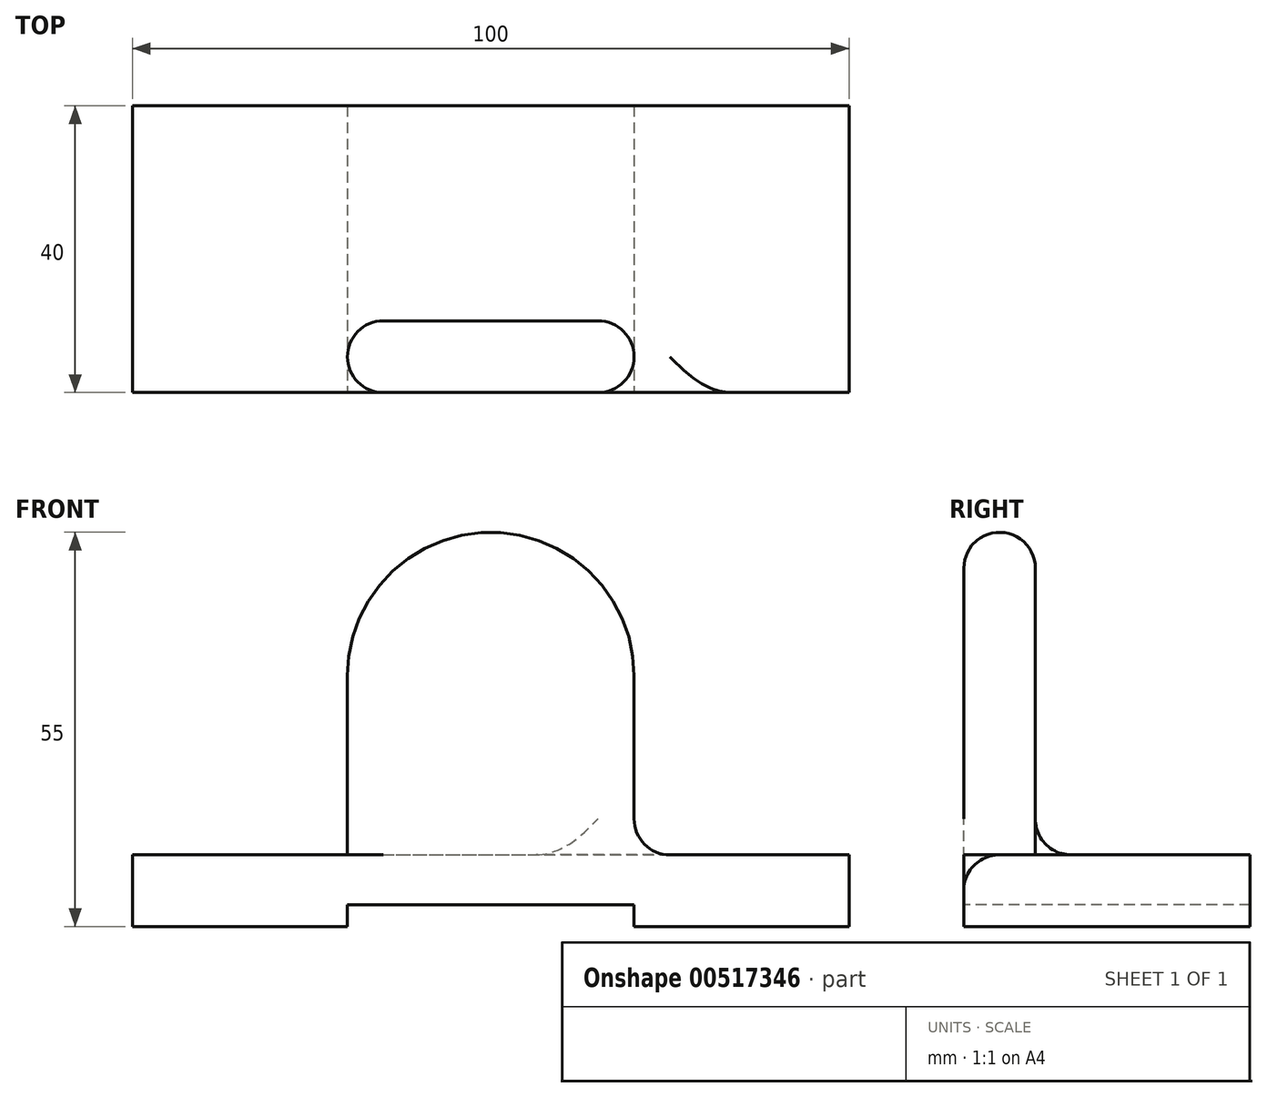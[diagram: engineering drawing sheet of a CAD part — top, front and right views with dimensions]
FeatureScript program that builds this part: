
annotation { "Feature Type Name" : "Feature", "Feature Type Description" : "" }
export const myFeature = defineFeature(function(context is Context, id is Id, definition is map)
    precondition{}
    {
        {
            var Q0;
            Q0=qCreatedBy(makeId("Top.planeOp"),FACE);
            var sketch = newSketch(context, id + "F0", { "sketchPlane" : qUnion([Q0])});
            skLineSegment(sketch, "E0.bottom", {"start": v(0, 0) * mm, "end": v(100, 0) * mm});
            skLineSegment(sketch, "E0.top", {"start": v(0, 40) * mm, "end": v(100, 40) * mm});
            skLineSegment(sketch, "E0.left", {"start": v(0, 0) * mm, "end": v(0, 40) * mm});
            skLineSegment(sketch, "E0.right", {"start": v(100, 0) * mm, "end": v(100, 40) * mm});
            skSolve(sketch);
        }
        {
            var Q0;
            Q0 = qSketchRegion(id + "F0", true);
            extrude(context, id + "F1", {"entities" : qUnion([Q0]), "depth" : 10 * mm, "offsetDistance" : 25 * mm});
        }
        {
            var Q0;
            Q0=makeQuery(id+"F1.opExtrude","SWEPT_FACE",FACE,{"disambiguationData":[OSD([sQuery(id+"F0.wireOp",EDGE,"E0.bottom")])]});
            var sketch = newSketch(context, id + "F2", { "sketchPlane" : qUnion([Q0])});
            skLineSegment(sketch, "E1", {"start": v(30, 0) * mm, "end": v(30, 35) * mm});
            skArc(sketch, "E2", {"start": v(30, 35) * mm, "mid": v(50, 55) * mm, "end": v(70, 35) * mm});
            skLineSegment(sketch, "E3", {"start": v(70, 35) * mm, "end": v(70, 0) * mm});
            skLineSegment(sketch, "E4", {"start": v(70, 0) * mm, "end": v(30, 0) * mm});
            skSolve(sketch);
        }
        {
            var Q0;
            Q0 = qSketchRegion(id + "F2", true);
            extrude(context, id + "F3", {"entities" : qUnion([Q0]), "operationType" : NewBodyOperationType.ADD, "oppositeDirection" : true, "depth" : 10 * mm, "offsetDistance" : 25 * mm});
        }
        {
            var Q0;
            Q0=makeQuery(id+"F3.boolean.opBoolean","MERGE",FACE,{"derivedFrom":[makeQuery(id+"F1.opExtrude","SWEPT_FACE",FACE,{"disambiguationData":[OSD([sQuery(id+"F0.wireOp",EDGE,"E0.bottom")])]}),makeQuery(id+"F3.opExtrude","CAP_FACE",FACE,{"disambiguationData":[OSD([sQuery(id+"F2.wireOp",EDGE,"E1"),sQuery(id+"F2.wireOp",EDGE,"E2"),sQuery(id+"F2.wireOp",EDGE,"E3"),sQuery(id+"F2.wireOp",EDGE,"E4")])],"isStart":true})]});
            var sketch = newSketch(context, id + "F4", { "sketchPlane" : qUnion([Q0])});
            skLineSegment(sketch, "E5.bottom", {"start": v(30, 0) * mm, "end": v(70, 0) * mm});
            skLineSegment(sketch, "E5.top", {"start": v(30, 3) * mm, "end": v(70, 3) * mm});
            skLineSegment(sketch, "E5.left", {"start": v(30, 0) * mm, "end": v(30, 3) * mm});
            skLineSegment(sketch, "E5.right", {"start": v(70, 0) * mm, "end": v(70, 3) * mm});
            skSolve(sketch);
        }
        {
            var Q0;
            Q0 = qSketchRegion(id + "F4", true);
            extrude(context, id + "F5", {"entities" : qUnion([Q0]), "operationType" : NewBodyOperationType.REMOVE, "endBound" : BoundingType.THROUGH_ALL, "oppositeDirection" : true, "depth" : 25 * mm, "offsetDistance" : 25 * mm});
        }
        {
            var Q0;
            Q0=makeQuery(id+"F3.opExtrude","SWEPT_FACE",FACE,{"disambiguationData":[OSD([sQuery(id+"F2.wireOp",EDGE,"E3")])]});
            fillet(context, id + "F6", {"entities" : qUnion([Q0]), "radius" : 5 * mm, "tangentPropagation" : true, "allowEdgeOverflow" : false});
        }
    });
